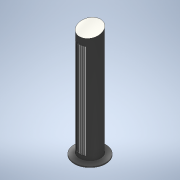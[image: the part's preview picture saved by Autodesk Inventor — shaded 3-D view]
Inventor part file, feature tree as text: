
AUTODESK INVENTOR PART (.ipt)
format: ipt  version: 2022 (Build 260153000, 153)  size: 193,024 bytes
history: native  units: mm
features: sketch x5, plane x3, extrude x3, loft x2, other x2, fillet x1, direct_edit x1
ambient origin geometry x8: Origin, YZ Plane, XZ Plane, XY Plane, X Axis, Y Axis, Z Axis, Center Point
bodies: Body1 (feature_tree)
feature tree (17):
  sketch  "Sketch1"  dims[d0=30.0mm d1=1.0mm]
  plane  "Work Plane1"
  sketch  "Sketch2"  dims[d2=30.0mm d3=1.0mm]
  plane  "Work Plane2"
  sketch  "Sketch4"  dims[d11=20.0mm d12=0.0mm d13=90.0deg]
  loft  "Loft2"
  loft  "Loft3"
  extrude  "Extrusion1"  TaperAngle=0.0deg  [1 undecoded]
  extrude  "Extrusion2"  TaperAngle=0.0deg  [1 undecoded]
  fillet  "Fillet1"  [1 undecoded]
  plane  "Work Plane3"
  extrude  "Extrusion3"  Depth=5.0mm
  direct_edit  "Direct Edit1"
  other  "Edges1"
  sketch  "Sketch5"  dims[d14=0.0mm d15=90.0deg d16=0.0mm d17=90.0deg d18=0.0mm d19=90.0deg]
  sketch  "Sketch6"  dims[d20=100.0mm d21=0.0mm d22=5.0mm d23=0.5mm d24=20.0mm d25=0.0mm d26=10.0mm d27=-10.0mm d28=90.0mm d29=10.0mm d30=10.0mm d31=5.0mm d32=5.0mm d33=0.0mm d34=1.0mm d35=0.5mm d36=1.0mm d37=0.5mm d38=1.0mm d39=0.5mm d40=1.0mm d41=0.5mm d42=1.0mm d43=0.5mm d44=1.0mm d45=1.0mm d46=0.5mm d47=5.0mm d48=10.0mm d49=10.0mm]
  other  "Scale1"
note: 3 required parameter values undecoded (feature->parameter linkage not recoverable at this tier; creation-order binding heuristic only, values carry confidence <= 0.55)
